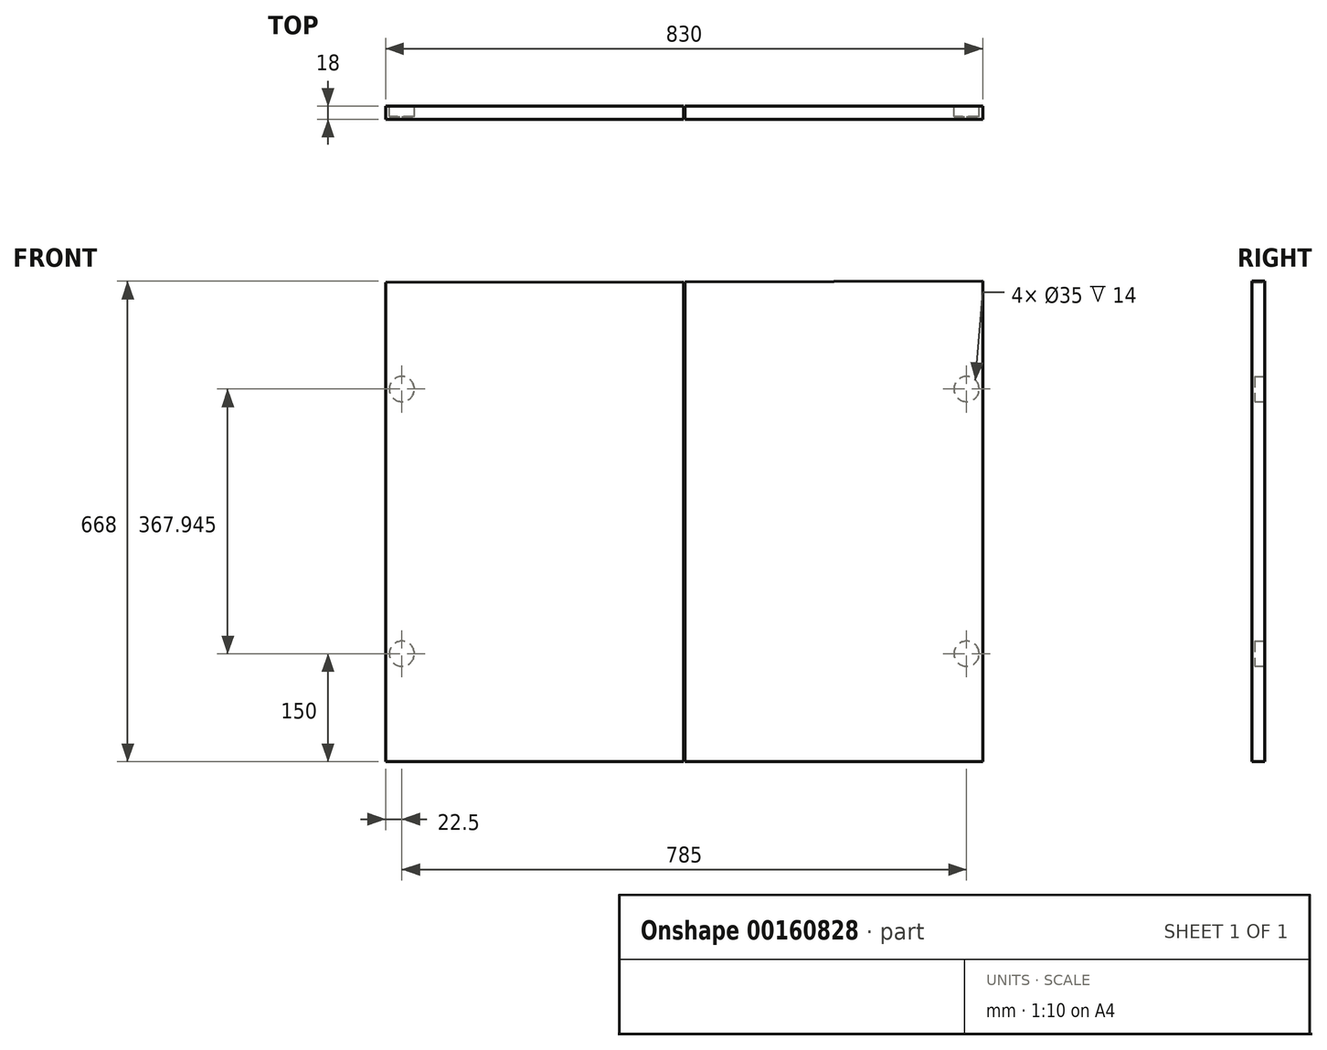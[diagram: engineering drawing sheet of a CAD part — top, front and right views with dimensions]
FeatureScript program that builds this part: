
annotation { "Feature Type Name" : "Feature", "Feature Type Description" : "" }
export const myFeature = defineFeature(function(context is Context, id is Id, definition is map)
    precondition{}
    {
        {
            var Q0;
            Q0=qCreatedBy(makeId("Front.planeOp"),FACE);
            var sketch = newSketch(context, id + "F0", { "sketchPlane" : qUnion([Q0])});
            skLineSegment(sketch, "E0", {"start": v(0, 0) * mm, "end": v(0, 10.42) * mm, "construction": true});
            skLineSegment(sketch, "E1.bottom", {"start": v(-415, 666) * mm, "end": v(-1, 667) * mm});
            skLineSegment(sketch, "E1.top", {"start": v(-415, 0) * mm, "end": v(-1, 0) * mm});
            skLineSegment(sketch, "E1.left", {"start": v(-415, 666) * mm, "end": v(-415, 0) * mm});
            skLineSegment(sketch, "E1.right", {"start": v(-1, 667) * mm, "end": v(-1, 0) * mm});
            skLineSegment(sketch, "E2.bottom", {"start": v(1, 667) * mm, "end": v(415, 668) * mm});
            skLineSegment(sketch, "E2.top", {"start": v(1, 0) * mm, "end": v(415, 0) * mm});
            skLineSegment(sketch, "E2.left", {"start": v(1, 667) * mm, "end": v(1, 0) * mm});
            skLineSegment(sketch, "E2.right", {"start": v(415, 668) * mm, "end": v(415, 0) * mm});
            skSolve(sketch);
        }
        {
            var Q0;
            Q0 = qSketchRegion(id + "F0", true);
            extrude(context, id + "F1", {"entities" : qUnion([Q0]), "depth" : 18 * mm});
        }
        {
            var Q0;
            Q0=makeQuery(id+"F1.opExtrude","CAP_FACE",FACE,{"disambiguationData":[OSD([sQuery(id+"F0.wireOp",EDGE,"E2.bottom"),sQuery(id+"F0.wireOp",EDGE,"E2.top"),sQuery(id+"F0.wireOp",EDGE,"E2.left"),sQuery(id+"F0.wireOp",EDGE,"E2.right")])],"isStart":true});
            var sketch = newSketch(context, id + "F2", { "sketchPlane" : qUnion([Q0])});
            skCircle(sketch, "E3", {"center": v(-392.5, 517.95) * mm, "radius": 17.5 * mm});
            skCircle(sketch, "E4", {"center": v(-392.5, 150) * mm, "radius": 17.5 * mm});
            skCircle(sketch, "E5", {"center": v(392.5, 517.95) * mm, "radius": 17.5 * mm});
            skCircle(sketch, "E6", {"center": v(392.5, 150) * mm, "radius": 17.5 * mm});
            skSolve(sketch);
        }
        {
            var Q0;
            Q0 = qSketchRegion(id + "F2", true);
            extrude(context, id + "F3", {"entities" : qUnion([Q0]), "operationType" : NewBodyOperationType.REMOVE, "oppositeDirection" : true, "depth" : 14 * mm});
        }
    });
